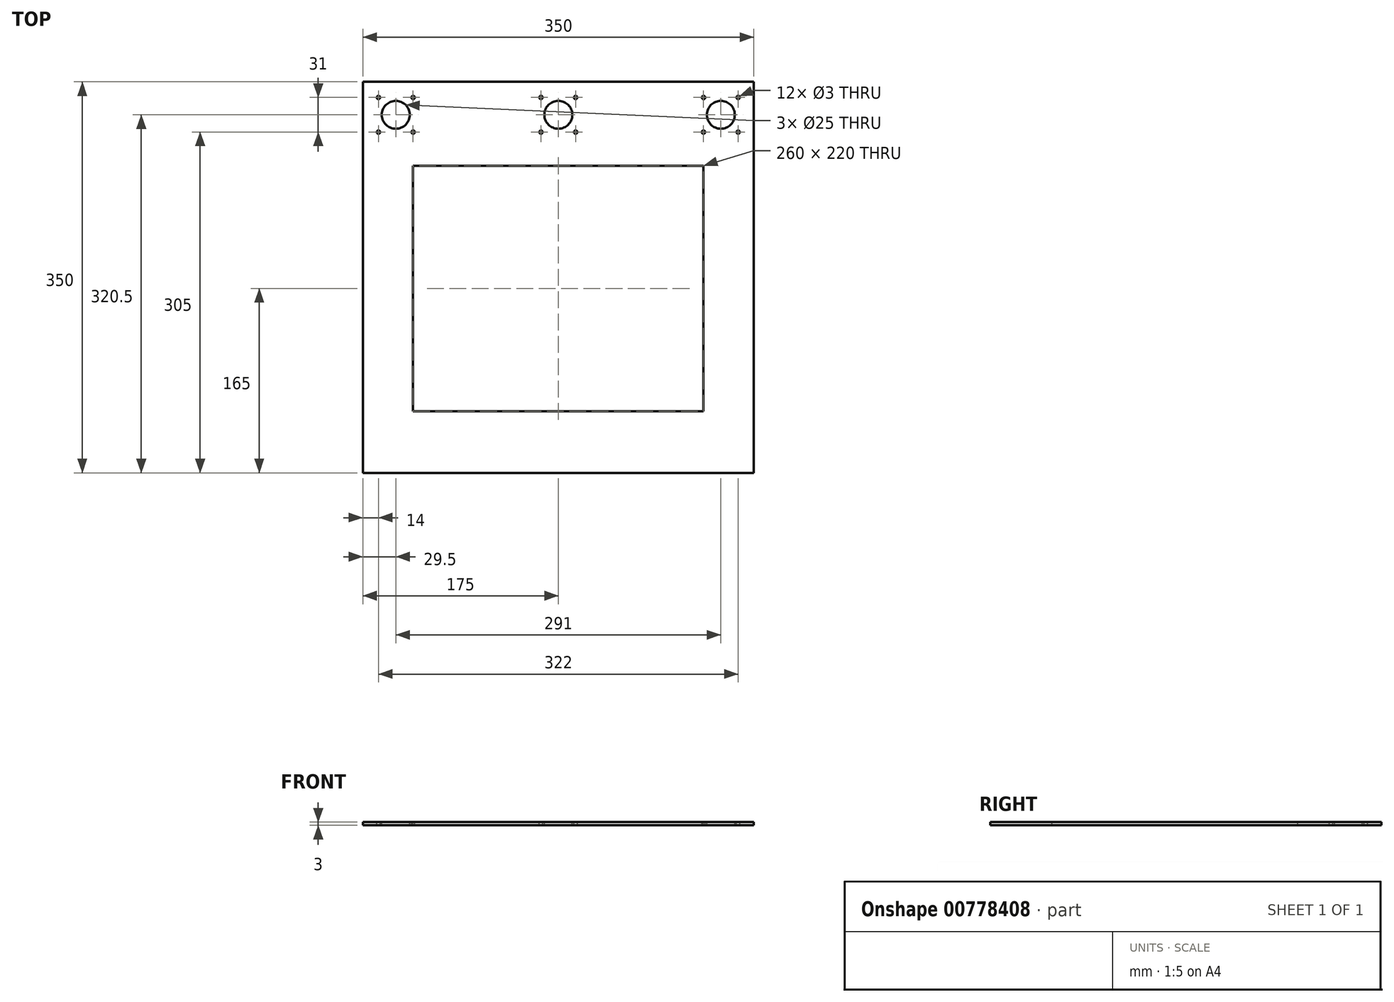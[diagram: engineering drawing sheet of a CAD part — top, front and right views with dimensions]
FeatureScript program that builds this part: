
annotation { "Feature Type Name" : "Feature", "Feature Type Description" : "" }
export const myFeature = defineFeature(function(context is Context, id is Id, definition is map)
    precondition{}
    {
        {
            var Q0;
            Q0=qCreatedBy(makeId("Top.planeOp"),FACE);
            var sketch = newSketch(context, id + "F0", { "sketchPlane" : qUnion([Q0])});
            skLineSegment(sketch, "E0.bottom", {"start": v(175, -175) * mm, "end": v(-175, -175) * mm});
            skLineSegment(sketch, "E0.top", {"start": v(175, 175) * mm, "end": v(-175, 175) * mm});
            skLineSegment(sketch, "E0.left", {"start": v(175, -175) * mm, "end": v(175, 175) * mm});
            skLineSegment(sketch, "E0.right", {"start": v(-175, -175) * mm, "end": v(-175, 175) * mm});
            skPoint(sketch, "E0.middle", {"position": v(0, 0) * mm});
            skSolve(sketch);
        }
        {
            var Q0;
            Q0 = qSketchRegion(id + "F0", true);
            extrude(context, id + "F1", {"entities" : qUnion([Q0]), "depth" : 3 * mm, "offsetDistance" : 25 * mm});
        }
        {
            var Q0;
            Q0=makeQuery(id+"F1.opExtrude","CAP_FACE",FACE,{"disambiguationData":[OSD([sQuery(id+"F0.wireOp",EDGE,"E0.bottom"),sQuery(id+"F0.wireOp",EDGE,"E0.top"),sQuery(id+"F0.wireOp",EDGE,"E0.left"),sQuery(id+"F0.wireOp",EDGE,"E0.right")])],"isStart":false});
            var sketch = newSketch(context, id + "F2", { "sketchPlane" : qUnion([Q0])});
            skLineSegment(sketch, "E1.bottom", {"start": v(130, -120) * mm, "end": v(-130, -120) * mm});
            skLineSegment(sketch, "E1.top", {"start": v(130, 100) * mm, "end": v(-130, 100) * mm});
            skLineSegment(sketch, "E1.left", {"start": v(130, -120) * mm, "end": v(130, 100) * mm});
            skLineSegment(sketch, "E1.right", {"start": v(-130, -120) * mm, "end": v(-130, 100) * mm});
            skPoint(sketch, "E1.middle", {"position": v(0, -10) * mm});
            skSolve(sketch);
        }
        {
            var Q0;
            Q0=makeQuery(id+"F2.imprint","IMPRINT",FACE,{"disambiguationData":[TD([[makeQuery(id+"F2.imprint","IMPRINT",EDGE,{"derivedFrom":sQuery(id+"F2.wireOp",EDGE,"E1.bottom")}),-1.0]])]});
            extrude(context, id + "F3", {"entities" : qUnion([Q0]), "operationType" : NewBodyOperationType.REMOVE, "oppositeDirection" : true, "depth" : 25 * mm, "offsetDistance" : 25 * mm});
        }
        {
            var Q0;
            Q0=makeQuery(id+"F1.opExtrude","CAP_FACE",FACE,{"disambiguationData":[OSD([sQuery(id+"F0.wireOp",EDGE,"E0.bottom"),sQuery(id+"F0.wireOp",EDGE,"E0.top"),sQuery(id+"F0.wireOp",EDGE,"E0.left"),sQuery(id+"F0.wireOp",EDGE,"E0.right")])],"isStart":false});
            var sketch = newSketch(context, id + "F4", { "sketchPlane" : qUnion([Q0])});
            skLineSegment(sketch, "E2.bottom", {"start": v(-161, 161) * mm, "end": v(-130, 161) * mm});
            skLineSegment(sketch, "E2.top", {"start": v(-161, 130) * mm, "end": v(-130, 130) * mm});
            skLineSegment(sketch, "E2.left", {"start": v(-161, 161) * mm, "end": v(-161, 130) * mm});
            skLineSegment(sketch, "E2.right", {"start": v(-130, 161) * mm, "end": v(-130, 130) * mm});
            skLineSegment(sketch, "E3.bottom", {"start": v(161, 161) * mm, "end": v(130, 161) * mm});
            skLineSegment(sketch, "E3.top", {"start": v(161, 130) * mm, "end": v(130, 130) * mm});
            skLineSegment(sketch, "E3.left", {"start": v(161, 161) * mm, "end": v(161, 130) * mm});
            skLineSegment(sketch, "E3.right", {"start": v(130, 161) * mm, "end": v(130, 130) * mm});
            skPoint(sketch, "E4", {"position": v(130, 161) * mm});
            skPoint(sketch, "E5", {"position": v(161, 130) * mm});
            skCircle(sketch, "E6", {"center": v(145.5, 145.5) * mm, "radius": 12.5 * mm});
            skCircle(sketch, "E7", {"center": v(-145.5, 145.5) * mm, "radius": 12.5 * mm});
            skLineSegment(sketch, "E8.bottom", {"start": v(-15.5, 161) * mm, "end": v(15.5, 161) * mm});
            skLineSegment(sketch, "E8.top", {"start": v(-15.5, 130) * mm, "end": v(15.5, 130) * mm});
            skLineSegment(sketch, "E8.left", {"start": v(-15.5, 161) * mm, "end": v(-15.5, 130) * mm});
            skLineSegment(sketch, "E8.right", {"start": v(15.5, 161) * mm, "end": v(15.5, 130) * mm});
            skCircle(sketch, "E9", {"center": v(0, 145.5) * mm, "radius": 12.5 * mm});
            skLineSegment(sketch, "E10", {"start": v(0, 175) * mm, "end": v(0, 100) * mm, "construction": true});
            skLineSegment(sketch, "E11", {"start": v(-145.5, 145.5) * mm, "end": v(145.5, 145.5) * mm, "construction": true});
            skSolve(sketch);
        }
        {
            var Q0;
            Q0=sQuery(id+"F4.wireOp",VERTEX,"E2.bottom.start");
            var Q1;
            Q1=sQuery(id+"F4.wireOp",VERTEX,"E2.top.start");
            var Q2;
            Q2=sQuery(id+"F4.wireOp",VERTEX,"E2.top.end");
            var Q3;
            Q3=sQuery(id+"F4.wireOp",VERTEX,"E2.bottom.end");
            var Q4;
            Q4=sQuery(id+"F4.wireOp",VERTEX,"E3.bottom.end");
            var Q5;
            Q5=sQuery(id+"F4.wireOp",VERTEX,"E3.bottom.start");
            var Q6;
            Q6=sQuery(id+"F4.wireOp",VERTEX,"E3.top.start");
            var Q7;
            Q7=sQuery(id+"F4.wireOp",VERTEX,"E3.top.end");
            var Q8;
            Q8=sQuery(id+"F4.wireOp",VERTEX,"E8.bottom.start");
            var Q9;
            Q9=sQuery(id+"F4.wireOp",VERTEX,"E8.top.start");
            var Q10;
            Q10=sQuery(id+"F4.wireOp",VERTEX,"E8.top.end");
            var Q11;
            Q11=sQuery(id+"F4.wireOp",VERTEX,"E8.bottom.end");
            var Q12;
            Q12=makeQuery(id+"F1.opExtrude","SWEPT_BODY",BODY,{"disambiguationData":[OSD([sQuery(id+"F0.wireOp",EDGE,"E0.bottom"),sQuery(id+"F0.wireOp",EDGE,"E0.top"),sQuery(id+"F0.wireOp",EDGE,"E0.left"),sQuery(id+"F0.wireOp",EDGE,"E0.right")])]});
            hole(context, id + "F5", {"style" : HoleStyle.SIMPLE, "endStyle" : HoleEndStyle.THROUGH, "holeDiameter" : 3 * mm, "majorDiameter" : 5 * mm, "isTappedThrough" : true, "tappedDepth" : 12 * mm, "tapClearance" : 3, "locations" : qUnion([Q0, Q1, Q2, Q3, Q4, Q5, Q6, Q7, Q8, Q9, Q10, Q11]), "scope" : qUnion([Q12])});
        }
        {
            var Q0;
            Q0=makeQuery(id+"F4.imprint","IMPRINT",FACE,{"disambiguationData":[TD([[makeQuery(id+"F4.imprint","IMPRINT",EDGE,{"derivedFrom":sQuery(id+"F4.wireOp",EDGE,"E7")}),1.0]])]});
            var Q1;
            Q1=makeQuery(id+"F4.imprint","IMPRINT",FACE,{"disambiguationData":[TD([[makeQuery(id+"F4.imprint","IMPRINT",EDGE,{"derivedFrom":sQuery(id+"F4.wireOp",EDGE,"E6")}),1.0]])]});
            var Q2;
            Q2=makeQuery(id+"F4.imprint","IMPRINT",FACE,{"disambiguationData":[TD([[makeQuery(id+"F4.imprint","IMPRINT",EDGE,{"derivedFrom":sQuery(id+"F4.wireOp",EDGE,"E9")}),1.0]])]});
            extrude(context, id + "F6", {"entities" : qUnion([Q0, Q1, Q2]), "operationType" : NewBodyOperationType.REMOVE, "oppositeDirection" : true, "depth" : 25 * mm, "offsetDistance" : 25 * mm});
        }
    });
